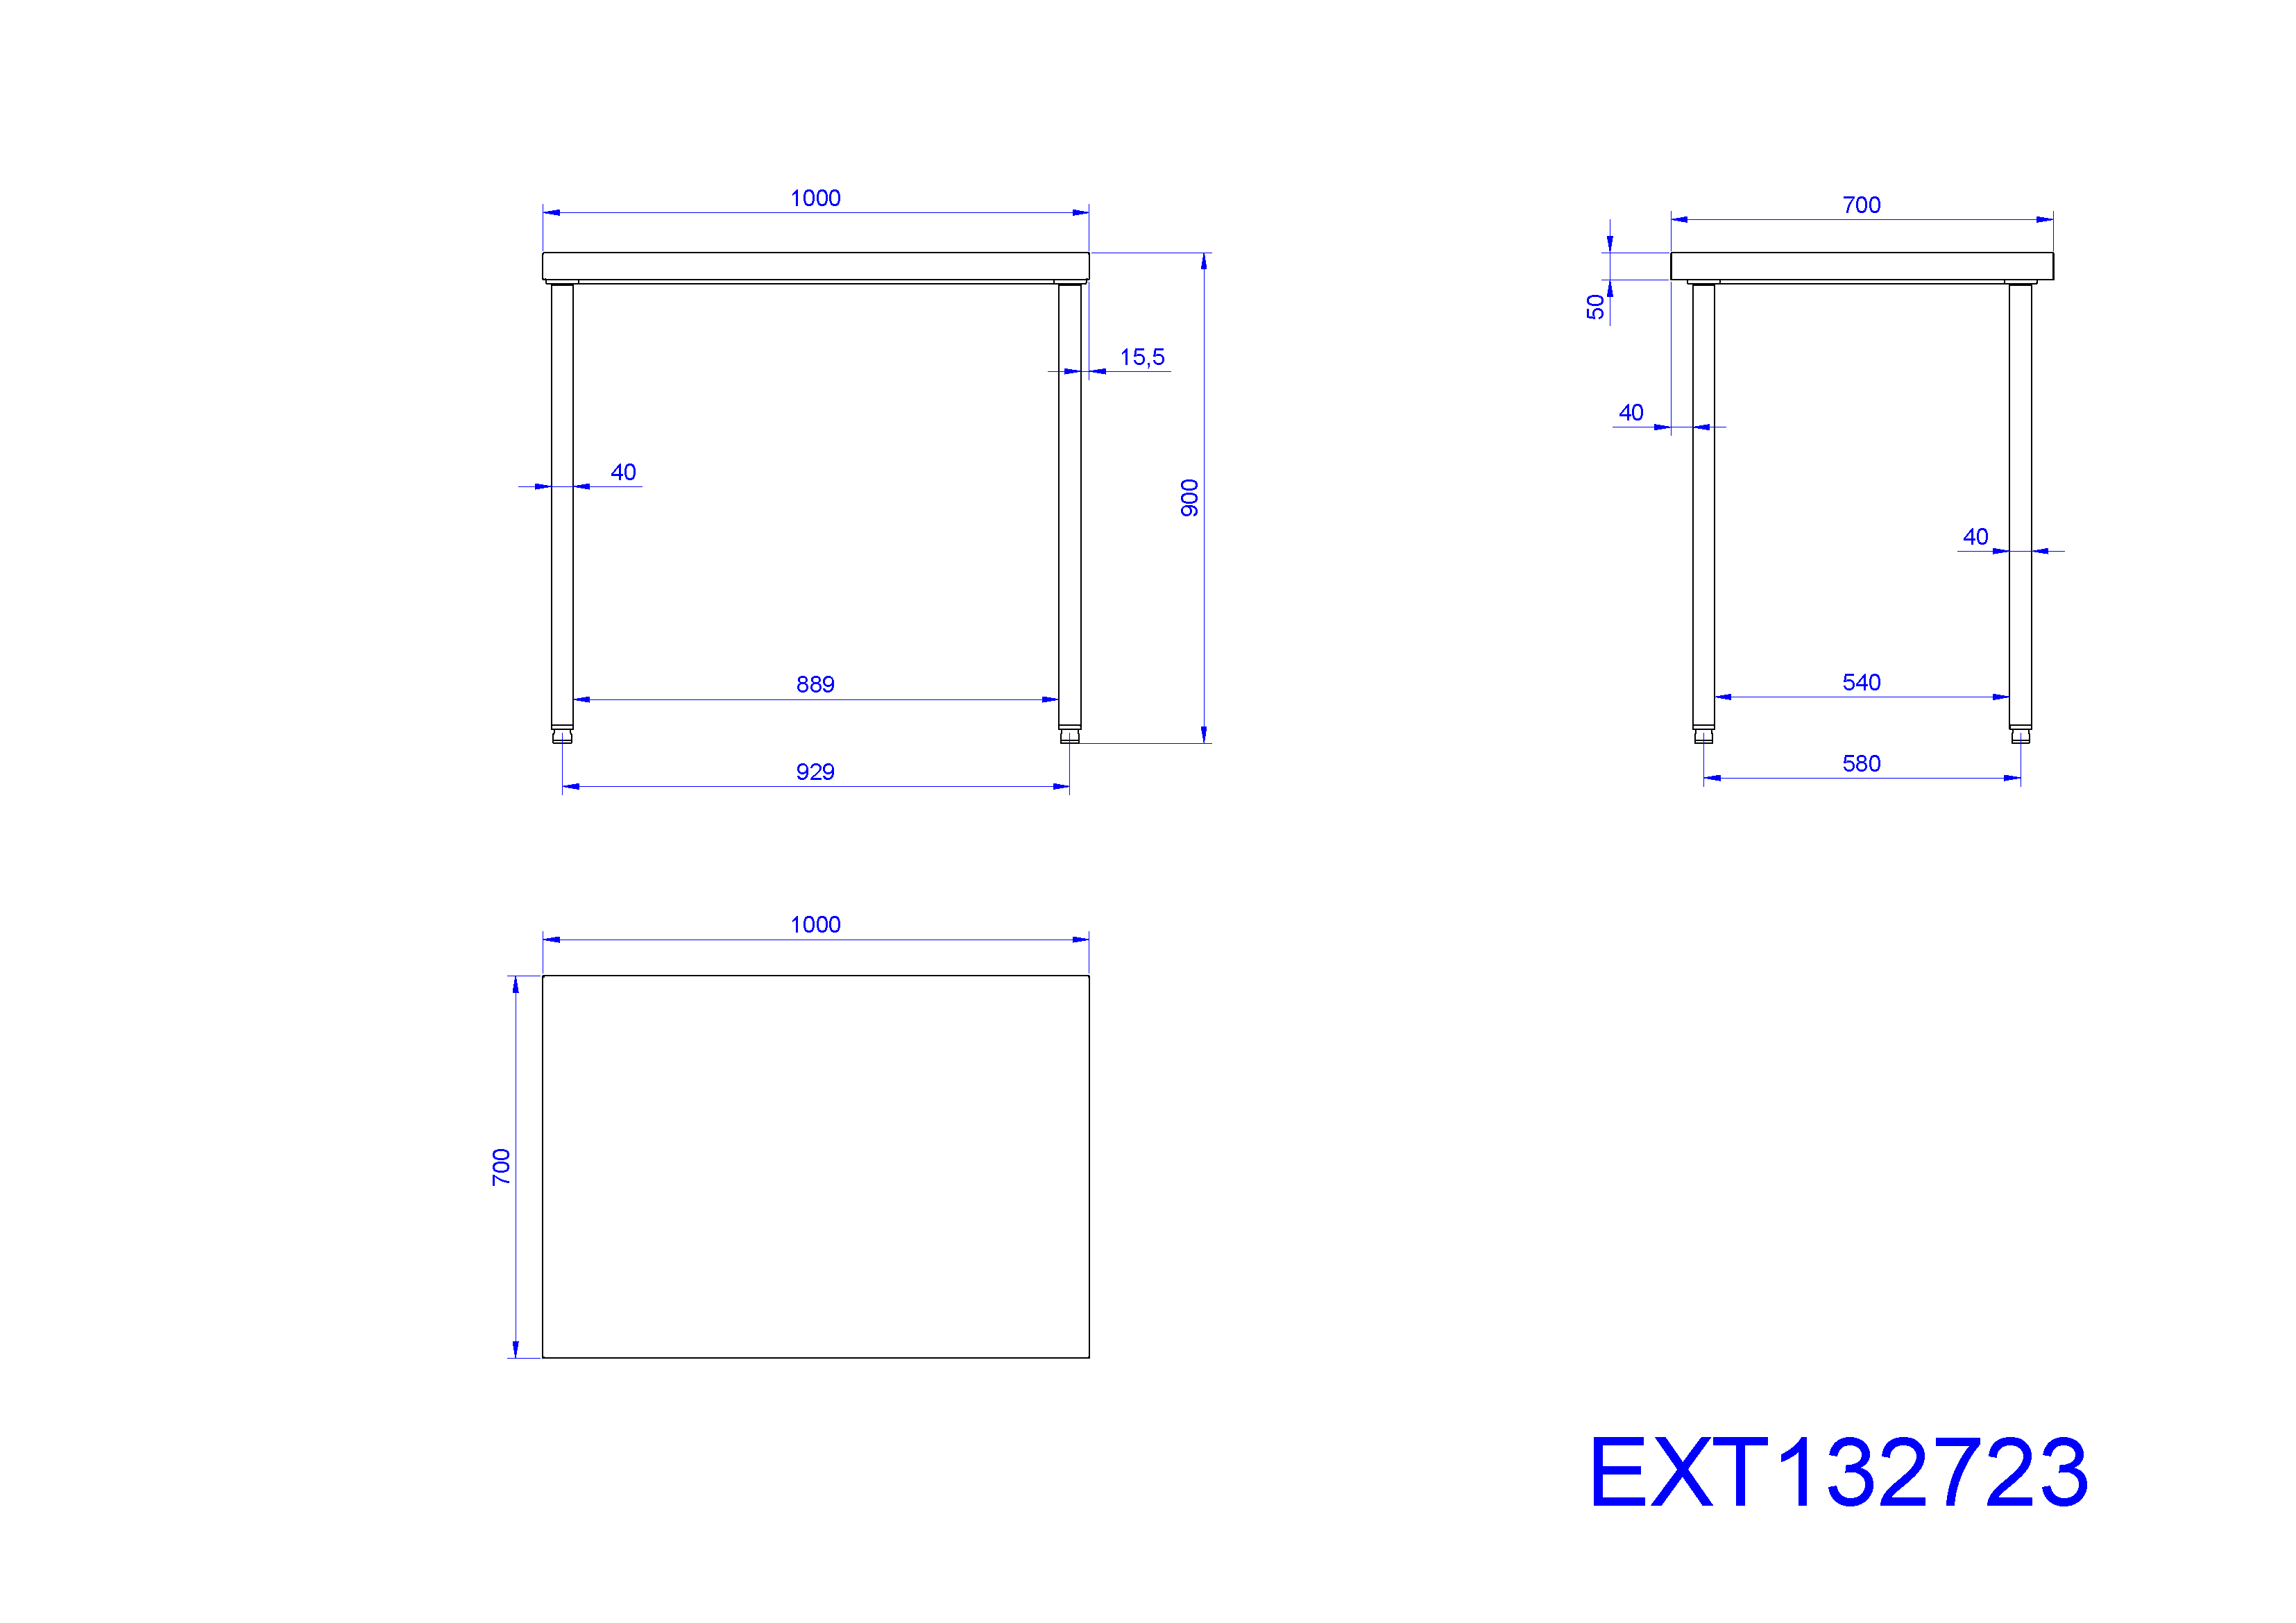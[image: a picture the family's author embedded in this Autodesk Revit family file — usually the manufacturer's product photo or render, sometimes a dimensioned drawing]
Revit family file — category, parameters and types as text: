
# Revit family: QF_ELECTROLUXPROFESSIONAL_132915_ML1B0717N
name_source: partatom
category: Attrezzature speciali
units: mm (PartAtom-declared; Revit-internal decimal feet)

## family parameters
Basato su piano di lavoro = No
Condiviso = No
Punto di calcolo locali = No
Quota connettore circolare = Usa diametro
Sempre verticale = Sì
Taglio con vuoti quando caricato = No
Tipo di parte = Normale

## types (1)
- Standard
    Accessory = Sì
    Cold Water Size = 0 mm
    Compressed Air Pressure = 0.0 Pa
    Compressed Air Size = 0 mm
    Compressed Air Volume = 0.0 L/s
    Condensate Return Size = 0 mm
    Cycle = 0 Hz
    Depth Actual = 700 mm  [stored 2.29659 ft]
    Descrizione = CUPBOARD SINK 1 BOWL (500X500) 700MM
    Direct Waste Size = 140 mm
    Gas Input Pressure = 0
    Gas KW = 0
    Gas Size = 0 mm
    HP = 0 HP
    Height Actual = 1000 mm  [stored 3.28084 ft]
    Hot Water Size = 0 mm
    Item Number = 132915
    Length Actual = 700 mm  [stored 2.29659 ft]
    Modello = ML1B0717N
    Phase = 0
    Produttore = Electrolux Professional
    Prospetto di default = 0 mm  [stored 0 ft]
    Refrigerant Compressor Remote = Sì
    Refrigeration Liquid Line Size = 0 mm  [stored 0 ft]
    Refrigeration Suction Line Size = 0 mm  [stored 0 ft]
    Steam Consumption per Hour = 0
    Steam Supply Maximum Pressure = 0.0 Pa
    Steam Supply Minimum Pressure = 0.0 Pa
    Steam Supply Size = 0 mm
    URL = https://www.electroluxprofessional.com
    URL Manufacturer = https://www.electroluxprofessional.com
    Volts = 0 V
    Watts = 0 W
    Weight = 40.00 kg

note: source unit labels omitted for Gas Input Pressure — the stored unit's dimension contradicts the parameter name (converter mislabeling)

note: [stored X ft] marks values corroborated as IEEE doubles in the binary element streams (Revit-internal decimal feet)

## geometry (parser evidence)
native form markers: Sweep x3
no freeform markers — native parametric forms only
